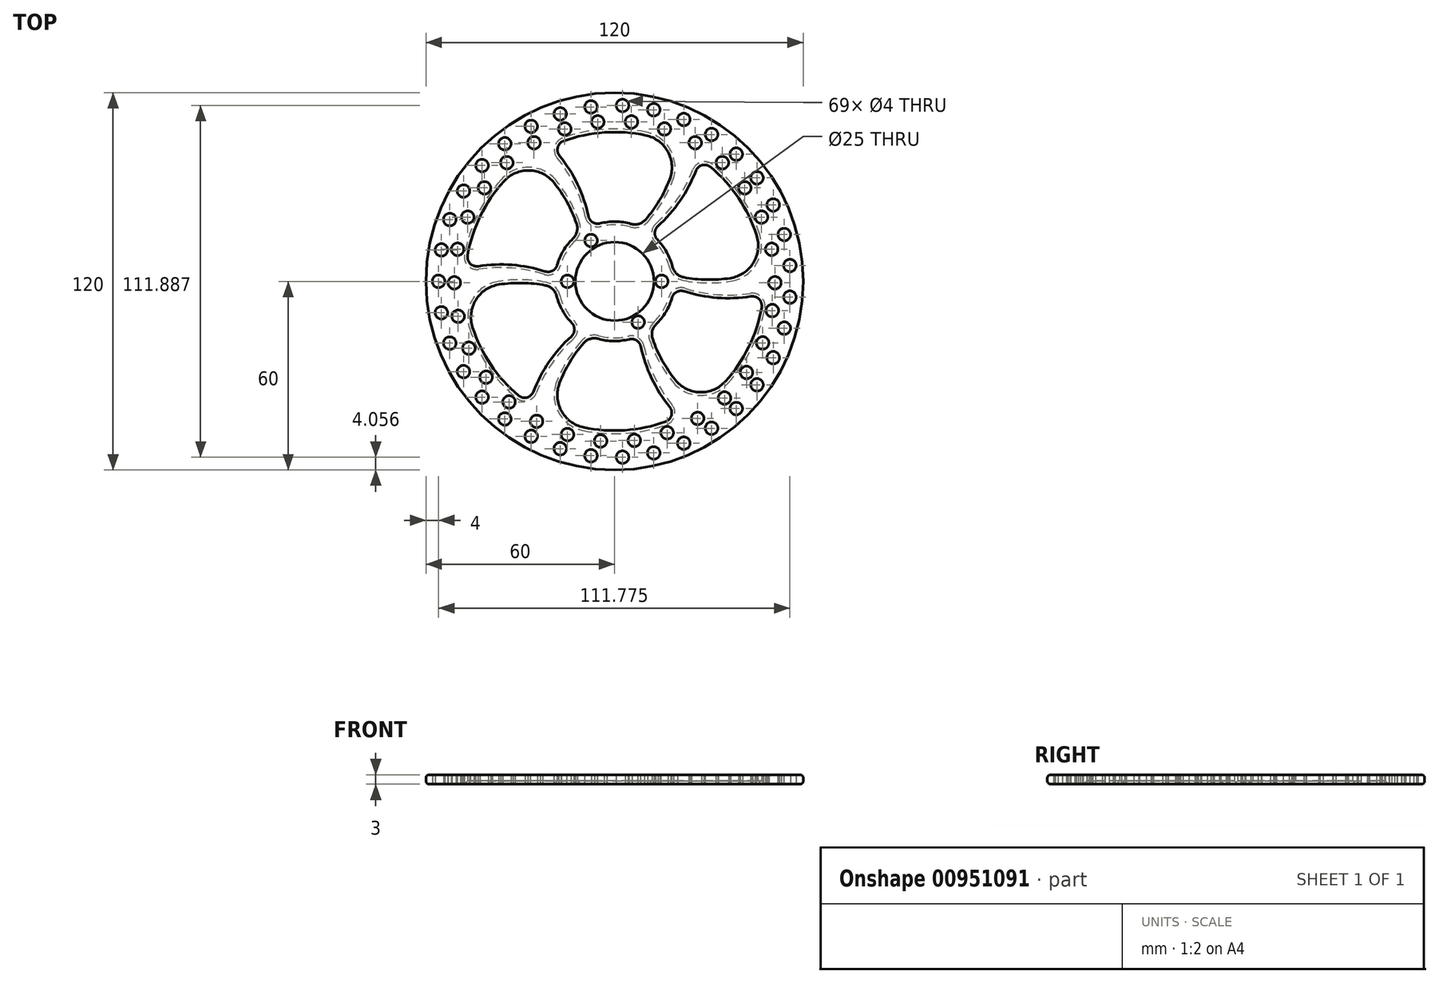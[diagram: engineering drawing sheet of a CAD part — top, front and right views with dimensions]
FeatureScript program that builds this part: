
annotation { "Feature Type Name" : "Feature", "Feature Type Description" : "" }
export const myFeature = defineFeature(function(context is Context, id is Id, definition is map)
    precondition{}
    {
        {
            var Q0;
            Q0=qCreatedBy(makeId("Top.planeOp"),FACE);
            var sketch = newSketch(context, id + "F0", { "sketchPlane" : qUnion([Q0])});
            skCircle(sketch, "E0", {"center": v(0, 0) * mm, "radius": 60 * mm});
            skCircle(sketch, "E1", {"center": v(0, 0) * mm, "radius": 10 * mm});
            skSolve(sketch);
        }
        {
            var Q0;
            Q0=makeQuery(id+"F0.imprint","IMPRINT",FACE,{"disambiguationData":[TD([[makeQuery(id+"F0.imprint","IMPRINT",EDGE,{"derivedFrom":sQuery(id+"F0.wireOp",EDGE,"E0")}),1.0]])]});
            extrude(context, id + "F1", {"entities" : qUnion([Q0]), "depth" : 3 * mm, "offsetDistance" : 25 * mm});
        }
        {
            var Q0;
            Q0=qCreatedBy(makeId("Top.planeOp"),FACE);
            var sketch = newSketch(context, id + "F2", { "sketchPlane" : qUnion([Q0])});
            skCircle(sketch, "E2.4.0", {"center": v(15, 0) * mm, "radius": 2 * mm});
            skPoint(sketch, "E2.center", {"position": v(0, 0) * mm});
            skCircle(sketch, "E3", {"center": v(0, 0) * mm, "radius": 12.5 * mm});
            skCircle(sketch, "E4", {"center": v(0, 0) * mm, "radius": 19 * mm});
            skCircle(sketch, "E5", {"center": v(0, 0) * mm, "radius": 47.5 * mm});
            skPoint(sketch, "E6.startSnap0", {"position": v(0, -18.25) * mm});
            skPoint(sketch, "E6.centerSnap0", {"position": v(0, -18.25) * mm});
            skArc(sketch, "E7", {"start": v(18.9, -2) * mm, "mid": v(32.95, -5.25) * mm, "end": v(47.33, -4) * mm});
            skPoint(sketch, "E8", {"position": v(47.5, 0) * mm});
            skPoint(sketch, "E9", {"position": v(19, 0) * mm});
            skArc(sketch, "E10", {"start": v(18.9, 2) * mm, "mid": v(33.28, 0.62) * mm, "end": v(47.33, 4) * mm});
            skArc(sketch, "E11.1.0", {"start": v(11.18, 15.36) * mm, "mid": v(21.02, 25.91) * mm, "end": v(27.13, 39) * mm});
            skArc(sketch, "E11.1.1", {"start": v(7.72, 17.36) * mm, "mid": v(16.1, 29.13) * mm, "end": v(20.2, 42.99) * mm});
            skArc(sketch, "E11.2.0", {"start": v(-7.72, 17.36) * mm, "mid": v(-11.93, 31.16) * mm, "end": v(-20.2, 43) * mm});
            skArc(sketch, "E11.2.1", {"start": v(-11.18, 15.36) * mm, "mid": v(-17.18, 28.5) * mm, "end": v(-27.13, 39) * mm});
            skArc(sketch, "E11.3.0", {"start": v(-18.9, 2) * mm, "mid": v(-32.95, 5.25) * mm, "end": v(-47.33, 4) * mm});
            skArc(sketch, "E11.3.1", {"start": v(-18.9, -2) * mm, "mid": v(-33.28, -0.62) * mm, "end": v(-47.33, -4) * mm});
            skArc(sketch, "E11.4.0", {"start": v(-11.18, -15.36) * mm, "mid": v(-21.02, -25.91) * mm, "end": v(-27.13, -39) * mm});
            skArc(sketch, "E11.4.1", {"start": v(-7.72, -17.36) * mm, "mid": v(-16.1, -29.13) * mm, "end": v(-20.2, -42.99) * mm});
            skArc(sketch, "E11.5.0", {"start": v(7.72, -17.36) * mm, "mid": v(11.93, -31.16) * mm, "end": v(20.2, -43) * mm});
            skArc(sketch, "E11.5.1", {"start": v(11.18, -15.36) * mm, "mid": v(17.18, -28.5) * mm, "end": v(27.13, -39) * mm});
            skCircle(sketch, "E12.1.0", {"center": v(7.5, -13) * mm, "radius": 2 * mm});
            skLineSegment(sketch, "E12.anchor1", {"start": v(0, 0) * mm, "end": v(15, 0) * mm, "construction": true});
            skLineSegment(sketch, "E12.anchor2", {"start": v(0, 0) * mm, "end": v(7.5, -13) * mm, "construction": true});
            skArc(sketch, "E13", {"start": v(-14.87, -2) * mm, "mid": v(-7.5, -13) * mm, "end": v(5.7, -13.87) * mm});
            skCircle(sketch, "E14", {"center": v(-15, 0) * mm, "radius": 2 * mm});
            skCircle(sketch, "E15.1.0", {"center": v(-7.5, 13) * mm, "radius": 2 * mm});
            skLineSegment(sketch, "E15.anchor1", {"start": v(0, 0) * mm, "end": v(-15, 0) * mm, "construction": true});
            skLineSegment(sketch, "E15.anchor2", {"start": v(0, 0) * mm, "end": v(-6.5, 11.26) * mm, "construction": true});
            skArc(sketch, "E16.trimOffspring", {"start": v(9.16, -11.88) * mm, "mid": v(13, -7.5) * mm, "end": v(14.87, -2) * mm});
            skArc(sketch, "E17.trimOffspring", {"start": v(14.87, 2) * mm, "mid": v(7.5, 13) * mm, "end": v(-5.7, 13.87) * mm});
            skArc(sketch, "E18.trimOffspring", {"start": v(-9.16, 11.88) * mm, "mid": v(-13, 7.5) * mm, "end": v(-14.87, 2) * mm});
            skSolve(sketch);
        }
        {
            var Q0;
            {var subQ0=sQuery(id+"F2.wireOp",EDGE,"E11.3.1");Q0=makeQuery(id+"F2.imprint","IMPRINT",FACE,{"disambiguationData":[TD([[makeQuery(id+"F2.imprint","IMPRINT",EDGE,{"derivedFrom":subQ0}),1.0]])]});}
            var Q1;
            {var subQ0=sQuery(id+"F2.wireOp",EDGE,"E11.4.1");Q1=makeQuery(id+"F2.imprint","IMPRINT",FACE,{"disambiguationData":[TD([[makeQuery(id+"F2.imprint","IMPRINT",EDGE,{"derivedFrom":subQ0}),1.0]])]});}
            var Q2;
            {var subQ0=sQuery(id+"F2.wireOp",EDGE,"E7");Q2=makeQuery(id+"F2.imprint","IMPRINT",FACE,{"disambiguationData":[TD([[makeQuery(id+"F2.imprint","IMPRINT",EDGE,{"derivedFrom":subQ0}),-1.0]])]});}
            var Q3;
            {var subQ0=sQuery(id+"F2.wireOp",EDGE,"E10");Q3=makeQuery(id+"F2.imprint","IMPRINT",FACE,{"disambiguationData":[TD([[makeQuery(id+"F2.imprint","IMPRINT",EDGE,{"derivedFrom":subQ0}),1.0]])]});}
            var Q4;
            {var subQ0=sQuery(id+"F2.wireOp",EDGE,"E11.1.1");Q4=makeQuery(id+"F2.imprint","IMPRINT",FACE,{"disambiguationData":[TD([[makeQuery(id+"F2.imprint","IMPRINT",EDGE,{"derivedFrom":subQ0}),1.0]])]});}
            var Q5;
            {var subQ0=sQuery(id+"F2.wireOp",EDGE,"E11.2.1");Q5=makeQuery(id+"F2.imprint","IMPRINT",FACE,{"disambiguationData":[TD([[makeQuery(id+"F2.imprint","IMPRINT",EDGE,{"derivedFrom":subQ0}),1.0]])]});}
            var Q6;
            {var subQ0=sQuery(id+"F2.wireOp",EDGE,"E3");var subQ12=sQuery(id+"F2.wireOp",EDGE,"4318ffa2-251d-41a1-aac9-47d39e21cad0.2.0");var subQ13=makeQuery(id+"F2.imprint","INTERSECT",VERTEX,{"disambiguationData":[OD(1.0)],"derivedFrom":[subQ12,subQ0]});Q6=makeQuery(id+"F2.imprint","IMPRINT",FACE,{"disambiguationData":[TD([[makeQuery(id+"F2.imprint","IMPRINT",EDGE,{"disambiguationData":[TD([[subQ13,-1.0]])],"derivedFrom":subQ0}),1.0]])]});}
            var Q7;
            Q7=makeQuery(id+"F0.imprint","IMPRINT",FACE,{"disambiguationData":[TD([[makeQuery(id+"F0.imprint","IMPRINT",EDGE,{"derivedFrom":sQuery(id+"F0.wireOp",EDGE,"E1")}),1.0]])]});
            extrude(context, id + "F3", {"entities" : qUnion([Q0, Q1, Q2, Q3, Q4, Q5, Q6, Q7]), "operationType" : NewBodyOperationType.REMOVE, "endBound" : BoundingType.SYMMETRIC, "depth" : 6 * mm, "offsetDistance" : 25 * mm});
        }
        {
            var Q0;
            Q0=qCreatedBy(makeId("Top.planeOp"),FACE);
            var sketch = newSketch(context, id + "F4", { "sketchPlane" : qUnion([Q0])});
            skPoint(sketch, "E19.center", {"position": v(0, 0) * mm});
            skLineSegment(sketch, "E20.anchor1", {"start": v(0, 0) * mm, "end": v(-49.05, 0) * mm, "construction": true});
            skLineSegment(sketch, "E20.anchor2", {"start": v(0, 0) * mm, "end": v(-41.78, -29.25) * mm, "construction": true});
            skCircle(sketch, "E21", {"center": v(-56, 0) * mm, "radius": 2 * mm});
            skCircle(sketch, "E22.1.0", {"center": v(-55.1, -10) * mm, "radius": 2 * mm});
            skCircle(sketch, "E22.2.0", {"center": v(-52.43, -19.68) * mm, "radius": 2 * mm});
            skCircle(sketch, "E22.3.0", {"center": v(-48.07, -28.72) * mm, "radius": 2 * mm});
            skCircle(sketch, "E22.4.0", {"center": v(-42.17, -36.84) * mm, "radius": 2 * mm});
            skCircle(sketch, "E22.5.0", {"center": v(-34.92, -43.78) * mm, "radius": 2 * mm});
            skCircle(sketch, "E22.6.0", {"center": v(-26.54, -49.31) * mm, "radius": 2 * mm});
            skCircle(sketch, "E22.7.0", {"center": v(-17.3, -53.26) * mm, "radius": 2 * mm});
            skCircle(sketch, "E22.8.0", {"center": v(-7.52, -55.5) * mm, "radius": 2 * mm});
            skCircle(sketch, "E22.9.0", {"center": v(2.51, -55.94) * mm, "radius": 2 * mm});
            skCircle(sketch, "E22.10.0", {"center": v(12.46, -54.6) * mm, "radius": 2 * mm});
            skCircle(sketch, "E22.11.0", {"center": v(22, -51.5) * mm, "radius": 2 * mm});
            skCircle(sketch, "E23.1.12.0", {"center": v(30.85, -46.74) * mm, "radius": 2 * mm});
            skCircle(sketch, "E23.1.13.0", {"center": v(38.7, -40.48) * mm, "radius": 2 * mm});
            skCircle(sketch, "E23.1.14.0", {"center": v(45.3, -32.92) * mm, "radius": 2 * mm});
            skCircle(sketch, "E24.1.15.0", {"center": v(50.45, -24.3) * mm, "radius": 2 * mm});
            skCircle(sketch, "E24.1.16.0", {"center": v(53.98, -14.9) * mm, "radius": 2 * mm});
            skCircle(sketch, "E24.1.17.0", {"center": v(55.77, -5.02) * mm, "radius": 2 * mm});
            skCircle(sketch, "E24.1.18.0", {"center": v(55.77, 5.02) * mm, "radius": 2 * mm});
            skCircle(sketch, "E24.1.19.0", {"center": v(53.98, 14.9) * mm, "radius": 2 * mm});
            skCircle(sketch, "E25.1.20.0", {"center": v(50.45, 24.3) * mm, "radius": 2 * mm});
            skCircle(sketch, "E25.1.21.0", {"center": v(45.3, 32.92) * mm, "radius": 2 * mm});
            skCircle(sketch, "E25.1.22.0", {"center": v(38.7, 40.48) * mm, "radius": 2 * mm});
            skCircle(sketch, "E26.1.23.0", {"center": v(30.85, 46.74) * mm, "radius": 2 * mm});
            skCircle(sketch, "E26.1.24.0", {"center": v(22, 51.5) * mm, "radius": 2 * mm});
            skCircle(sketch, "E27.1.25.0", {"center": v(12.46, 54.6) * mm, "radius": 2 * mm});
            skCircle(sketch, "E27.1.26.0", {"center": v(2.51, 55.94) * mm, "radius": 2 * mm});
            skCircle(sketch, "E28.1.27.0", {"center": v(-7.52, 55.5) * mm, "radius": 2 * mm});
            skCircle(sketch, "E28.1.28.0", {"center": v(-17.3, 53.26) * mm, "radius": 2 * mm});
            skCircle(sketch, "E28.1.29.0", {"center": v(-26.54, 49.31) * mm, "radius": 2 * mm});
            skCircle(sketch, "E29.1.30.0", {"center": v(-34.92, 43.78) * mm, "radius": 2 * mm});
            skCircle(sketch, "E29.1.31.0", {"center": v(-42.17, 36.84) * mm, "radius": 2 * mm});
            skCircle(sketch, "E29.1.32.0", {"center": v(-48.07, 28.72) * mm, "radius": 2 * mm});
            skCircle(sketch, "E29.1.33.0", {"center": v(-52.43, 19.68) * mm, "radius": 2 * mm});
            skCircle(sketch, "E29.1.34.0", {"center": v(-55.1, 10) * mm, "radius": 2 * mm});
            skCircle(sketch, "E30.1.17.0", {"center": v(50.14, -9.3) * mm, "radius": 2 * mm});
            skCircle(sketch, "E31.1.0", {"center": v(47.09, -19.59) * mm, "radius": 2 * mm});
            skCircle(sketch, "E31.2.0", {"center": v(41.95, -29) * mm, "radius": 2 * mm});
            skCircle(sketch, "E31.3.0", {"center": v(34.96, -37.13) * mm, "radius": 2 * mm});
            skCircle(sketch, "E31.4.0", {"center": v(26.42, -43.62) * mm, "radius": 2 * mm});
            skCircle(sketch, "E31.5.0", {"center": v(16.72, -48.18) * mm, "radius": 2 * mm});
            skCircle(sketch, "E31.6.0", {"center": v(6.28, -50.61) * mm, "radius": 2 * mm});
            skCircle(sketch, "E31.7.0", {"center": v(-4.44, -50.8) * mm, "radius": 2 * mm});
            skCircle(sketch, "E31.8.0", {"center": v(-14.97, -48.75) * mm, "radius": 2 * mm});
            skCircle(sketch, "E31.9.0", {"center": v(-24.83, -44.55) * mm, "radius": 2 * mm});
            skCircle(sketch, "E31.10.0", {"center": v(-33.6, -38.37) * mm, "radius": 2 * mm});
            skCircle(sketch, "E31.11.0", {"center": v(-40.88, -30.5) * mm, "radius": 2 * mm});
            skCircle(sketch, "E31.12.0", {"center": v(-46.35, -21.27) * mm, "radius": 2 * mm});
            skCircle(sketch, "E31.13.0", {"center": v(-49.77, -11.11) * mm, "radius": 2 * mm});
            skCircle(sketch, "E31.14.0", {"center": v(-51, -0.46) * mm, "radius": 2 * mm});
            skCircle(sketch, "E31.15.0", {"center": v(-49.97, 10.21) * mm, "radius": 2 * mm});
            skCircle(sketch, "E31.16.0", {"center": v(-46.73, 20.43) * mm, "radius": 2 * mm});
            skCircle(sketch, "E31.17.0", {"center": v(-41.42, 29.75) * mm, "radius": 2 * mm});
            skCircle(sketch, "E31.18.0", {"center": v(-34.29, 37.76) * mm, "radius": 2 * mm});
            skCircle(sketch, "E31.19.0", {"center": v(-25.63, 44.1) * mm, "radius": 2 * mm});
            skCircle(sketch, "E31.20.0", {"center": v(-15.85, 48.48) * mm, "radius": 2 * mm});
            skCircle(sketch, "E31.21.0", {"center": v(-5.36, 50.72) * mm, "radius": 2 * mm});
            skCircle(sketch, "E31.22.0", {"center": v(5.36, 50.72) * mm, "radius": 2 * mm});
            skCircle(sketch, "E31.23.0", {"center": v(15.85, 48.48) * mm, "radius": 2 * mm});
            skCircle(sketch, "E31.24.0", {"center": v(25.63, 44.1) * mm, "radius": 2 * mm});
            skCircle(sketch, "E31.25.0", {"center": v(34.29, 37.76) * mm, "radius": 2 * mm});
            skCircle(sketch, "E31.26.0", {"center": v(41.42, 29.75) * mm, "radius": 2 * mm});
            skCircle(sketch, "E31.27.0", {"center": v(46.73, 20.43) * mm, "radius": 2 * mm});
            skCircle(sketch, "E31.28.0", {"center": v(49.97, 10.21) * mm, "radius": 2 * mm});
            skCircle(sketch, "E31.29.0", {"center": v(51, -0.46) * mm, "radius": 2 * mm});
            skLineSegment(sketch, "E31.anchor1", {"start": v(0, 0) * mm, "end": v(50.14, -9.3) * mm, "construction": true});
            skLineSegment(sketch, "E31.anchor2", {"start": v(0, 0) * mm, "end": v(51, -0.46) * mm, "construction": true});
            skSolve(sketch);
        }
        {
            var Q0;
            Q0 = qSketchRegion(id + "F4", true);
            extrude(context, id + "F5", {"entities" : qUnion([Q0]), "operationType" : NewBodyOperationType.REMOVE, "endBound" : BoundingType.UP_TO_NEXT, "depth" : 25 * mm, "offsetDistance" : 25 * mm});
        }
        {
            var Q0;
            Q0=makeQuery(id+"F3.boolean.opBoolean","COPY",EDGE,{"derivedFrom":makeQuery(id+"F3.opExtrude","SWEPT_EDGE",EDGE,{"disambiguationData":[OSD([sQuery(id+"F2.wireOp",EDGE,"E5"),sQuery(id+"F2.wireOp",EDGE,"E11.3.0")])]})});
            var Q1;
            Q1=makeQuery(id+"F3.boolean.opBoolean","COPY",EDGE,{"derivedFrom":makeQuery(id+"F3.opExtrude","SWEPT_EDGE",EDGE,{"disambiguationData":[OSD([sQuery(id+"F2.wireOp",EDGE,"E4"),sQuery(id+"F2.wireOp",EDGE,"E11.3.0")])]})});
            var Q2;
            Q2=makeQuery(id+"F3.boolean.opBoolean","COPY",EDGE,{"derivedFrom":makeQuery(id+"F3.opExtrude","SWEPT_EDGE",EDGE,{"disambiguationData":[OSD([sQuery(id+"F2.wireOp",EDGE,"E4"),sQuery(id+"F2.wireOp",EDGE,"E11.2.0")])]})});
            var Q3;
            Q3=makeQuery(id+"F3.boolean.opBoolean","COPY",EDGE,{"derivedFrom":makeQuery(id+"F3.opExtrude","SWEPT_EDGE",EDGE,{"disambiguationData":[OSD([sQuery(id+"F2.wireOp",EDGE,"E5"),sQuery(id+"F2.wireOp",EDGE,"E11.2.0")])]})});
            var Q4;
            Q4=makeQuery(id+"F3.boolean.opBoolean","COPY",EDGE,{"derivedFrom":makeQuery(id+"F3.opExtrude","SWEPT_EDGE",EDGE,{"disambiguationData":[OSD([sQuery(id+"F2.wireOp",EDGE,"E5"),sQuery(id+"F2.wireOp",EDGE,"E11.1.0")])]})});
            var Q5;
            Q5=makeQuery(id+"F3.boolean.opBoolean","COPY",EDGE,{"derivedFrom":makeQuery(id+"F3.opExtrude","SWEPT_EDGE",EDGE,{"disambiguationData":[OSD([sQuery(id+"F2.wireOp",EDGE,"E4"),sQuery(id+"F2.wireOp",EDGE,"E11.1.0")])]})});
            var Q6;
            Q6=makeQuery(id+"F3.boolean.opBoolean","COPY",EDGE,{"derivedFrom":makeQuery(id+"F3.opExtrude","SWEPT_EDGE",EDGE,{"disambiguationData":[OSD([sQuery(id+"F2.wireOp",EDGE,"E4"),sQuery(id+"F2.wireOp",EDGE,"E7")])]})});
            var Q7;
            Q7=makeQuery(id+"F3.boolean.opBoolean","COPY",EDGE,{"derivedFrom":makeQuery(id+"F3.opExtrude","SWEPT_EDGE",EDGE,{"disambiguationData":[OSD([sQuery(id+"F2.wireOp",EDGE,"E5"),sQuery(id+"F2.wireOp",EDGE,"E7")])]})});
            var Q8;
            Q8=makeQuery(id+"F3.boolean.opBoolean","COPY",EDGE,{"derivedFrom":makeQuery(id+"F3.opExtrude","SWEPT_EDGE",EDGE,{"disambiguationData":[OSD([sQuery(id+"F2.wireOp",EDGE,"E4"),sQuery(id+"F2.wireOp",EDGE,"E11.5.0")])]})});
            var Q9;
            Q9=makeQuery(id+"F3.boolean.opBoolean","COPY",EDGE,{"derivedFrom":makeQuery(id+"F3.opExtrude","SWEPT_EDGE",EDGE,{"disambiguationData":[OSD([sQuery(id+"F2.wireOp",EDGE,"E5"),sQuery(id+"F2.wireOp",EDGE,"E11.5.0")])]})});
            var Q10;
            Q10=makeQuery(id+"F3.boolean.opBoolean","COPY",EDGE,{"derivedFrom":makeQuery(id+"F3.opExtrude","SWEPT_EDGE",EDGE,{"disambiguationData":[OSD([sQuery(id+"F2.wireOp",EDGE,"E4"),sQuery(id+"F2.wireOp",EDGE,"E11.4.0")])]})});
            var Q11;
            Q11=makeQuery(id+"F3.boolean.opBoolean","COPY",EDGE,{"derivedFrom":makeQuery(id+"F3.opExtrude","SWEPT_EDGE",EDGE,{"disambiguationData":[OSD([sQuery(id+"F2.wireOp",EDGE,"E5"),sQuery(id+"F2.wireOp",EDGE,"E11.4.0")])]})});
            fillet(context, id + "F6", {"entities" : qUnion([Q0, Q1, Q2, Q3, Q4, Q5, Q6, Q7, Q8, Q9, Q10, Q11]), "radius" : 3 * mm, "tangentPropagation" : true, "allowEdgeOverflow" : false});
        }
        {
            var Q0;
            Q0=makeQuery(id+"F3.boolean.opBoolean","COPY",EDGE,{"derivedFrom":makeQuery(id+"F3.opExtrude","SWEPT_EDGE",EDGE,{"disambiguationData":[OSD([sQuery(id+"F2.wireOp",EDGE,"E5"),sQuery(id+"F2.wireOp",EDGE,"E11.4.1")])]})});
            var Q1;
            Q1=makeQuery(id+"F3.boolean.opBoolean","COPY",EDGE,{"derivedFrom":makeQuery(id+"F3.opExtrude","SWEPT_EDGE",EDGE,{"disambiguationData":[OSD([sQuery(id+"F2.wireOp",EDGE,"E5"),sQuery(id+"F2.wireOp",EDGE,"E11.5.1")])]})});
            var Q2;
            Q2=makeQuery(id+"F3.boolean.opBoolean","COPY",EDGE,{"derivedFrom":makeQuery(id+"F3.opExtrude","SWEPT_EDGE",EDGE,{"disambiguationData":[OSD([sQuery(id+"F2.wireOp",EDGE,"E5"),sQuery(id+"F2.wireOp",EDGE,"E10")])]})});
            var Q3;
            Q3=makeQuery(id+"F3.boolean.opBoolean","COPY",EDGE,{"derivedFrom":makeQuery(id+"F3.opExtrude","SWEPT_EDGE",EDGE,{"disambiguationData":[OSD([sQuery(id+"F2.wireOp",EDGE,"E5"),sQuery(id+"F2.wireOp",EDGE,"E11.1.1")])]})});
            var Q4;
            Q4=makeQuery(id+"F3.boolean.opBoolean","COPY",EDGE,{"derivedFrom":makeQuery(id+"F3.opExtrude","SWEPT_EDGE",EDGE,{"disambiguationData":[OSD([sQuery(id+"F2.wireOp",EDGE,"E5"),sQuery(id+"F2.wireOp",EDGE,"E11.2.1")])]})});
            var Q5;
            Q5=makeQuery(id+"F3.boolean.opBoolean","COPY",EDGE,{"derivedFrom":makeQuery(id+"F3.opExtrude","SWEPT_EDGE",EDGE,{"disambiguationData":[OSD([sQuery(id+"F2.wireOp",EDGE,"E5"),sQuery(id+"F2.wireOp",EDGE,"E11.3.1")])]})});
            fillet(context, id + "F7", {"entities" : qUnion([Q0, Q1, Q2, Q3, Q4, Q5]), "radius" : 10.5 * mm, "tangentPropagation" : true, "allowEdgeOverflow" : false});
        }
        {
            var Q0;
            Q0=makeQuery(id+"F3.boolean.opBoolean","COPY",EDGE,{"derivedFrom":makeQuery(id+"F3.opExtrude","SWEPT_EDGE",EDGE,{"disambiguationData":[OSD([sQuery(id+"F2.wireOp",EDGE,"E4"),sQuery(id+"F2.wireOp",EDGE,"E11.3.1")])]})});
            var Q1;
            Q1=makeQuery(id+"F3.boolean.opBoolean","COPY",EDGE,{"derivedFrom":makeQuery(id+"F3.opExtrude","SWEPT_EDGE",EDGE,{"disambiguationData":[OSD([sQuery(id+"F2.wireOp",EDGE,"E4"),sQuery(id+"F2.wireOp",EDGE,"E11.4.1")])]})});
            var Q2;
            Q2=makeQuery(id+"F3.boolean.opBoolean","COPY",EDGE,{"derivedFrom":makeQuery(id+"F3.opExtrude","SWEPT_EDGE",EDGE,{"disambiguationData":[OSD([sQuery(id+"F2.wireOp",EDGE,"E4"),sQuery(id+"F2.wireOp",EDGE,"E11.5.1")])]})});
            var Q3;
            Q3=makeQuery(id+"F3.boolean.opBoolean","COPY",EDGE,{"derivedFrom":makeQuery(id+"F3.opExtrude","SWEPT_EDGE",EDGE,{"disambiguationData":[OSD([sQuery(id+"F2.wireOp",EDGE,"E4"),sQuery(id+"F2.wireOp",EDGE,"E10")])]})});
            var Q4;
            Q4=makeQuery(id+"F3.boolean.opBoolean","COPY",EDGE,{"derivedFrom":makeQuery(id+"F3.opExtrude","SWEPT_EDGE",EDGE,{"disambiguationData":[OSD([sQuery(id+"F2.wireOp",EDGE,"E4"),sQuery(id+"F2.wireOp",EDGE,"E11.1.1")])]})});
            var Q5;
            Q5=makeQuery(id+"F3.boolean.opBoolean","COPY",EDGE,{"derivedFrom":makeQuery(id+"F3.opExtrude","SWEPT_EDGE",EDGE,{"disambiguationData":[OSD([sQuery(id+"F2.wireOp",EDGE,"E4"),sQuery(id+"F2.wireOp",EDGE,"E11.2.1")])]})});
            fillet(context, id + "F8", {"entities" : qUnion([Q0, Q1, Q2, Q3, Q4, Q5]), "radius" : 4.5 * mm, "tangentPropagation" : true, "allowEdgeOverflow" : false});
        }
        {
            var Q0;
            Q0=makeQuery(id+"F1.opExtrude","CAP_EDGE",EDGE,{"disambiguationData":[OSD([sQuery(id+"F0.wireOp",EDGE,"E0")])],"isStart":true});
            fillet(context, id + "F9", {"entities" : qUnion([Q0]), "radius" : 1 * mm, "tangentPropagation" : true, "allowEdgeOverflow" : false});
        }
        {
            var Q0;
            Q0=makeQuery(id+"F1.opExtrude","CAP_EDGE",EDGE,{"disambiguationData":[OSD([sQuery(id+"F0.wireOp",EDGE,"E0")])],"isStart":false});
            fillet(context, id + "F10", {"entities" : qUnion([Q0]), "radius" : 1 * mm, "tangentPropagation" : true, "allowEdgeOverflow" : false});
        }
        {
            var Q0;
            {var subQ0=sQuery(id+"F2.wireOp",EDGE,"E5");Q0=makeQuery(id+"F3.boolean.opBoolean","INTERSECT",EDGE,{"derivedFrom":[makeQuery(id+"F1.opExtrude","CAP_FACE",FACE,{"disambiguationData":[OSD([sQuery(id+"F0.wireOp",EDGE,"E0"),sQuery(id+"F0.wireOp",EDGE,"E1")])],"isStart":true}),makeQuery(id+"F3.opExtrude","SWEPT_FACE",FACE,{"disambiguationData":[OSD([subQ0]),TDD([makeQuery(id+"F2.imprint","IMPRINT",EDGE,{"disambiguationData":[TD([[makeQuery(id+"F2.imprint","INTERSECT",VERTEX,{"derivedFrom":[subQ0,sQuery(id+"F2.wireOp",EDGE,"E7")]}),1.0]])],"derivedFrom":subQ0})])]})]});}
            chamfer(context, id + "F11", {"entities" : qUnion([Q0]), "width" : 1 * mm, "tangentPropagation" : true});
        }
        {
            var Q0;
            {var subQ0=sQuery(id+"F2.wireOp",EDGE,"E5");Q0=makeQuery(id+"F3.boolean.opBoolean","INTERSECT",EDGE,{"derivedFrom":[makeQuery(id+"F1.opExtrude","CAP_FACE",FACE,{"disambiguationData":[OSD([sQuery(id+"F0.wireOp",EDGE,"E0"),sQuery(id+"F0.wireOp",EDGE,"E1")])],"isStart":true}),makeQuery(id+"F3.opExtrude","SWEPT_FACE",FACE,{"disambiguationData":[OSD([subQ0]),TDD([makeQuery(id+"F2.imprint","IMPRINT",EDGE,{"disambiguationData":[TD([[makeQuery(id+"F2.imprint","INTERSECT",VERTEX,{"derivedFrom":[subQ0,sQuery(id+"F2.wireOp",EDGE,"E11.4.1")]}),-1.0]])],"derivedFrom":subQ0})])]})]});}
            var Q1;
            Q1=makeQuery(id+"F3.boolean.opBoolean","INTERSECT",EDGE,{"derivedFrom":[makeQuery(id+"F1.opExtrude","CAP_FACE",FACE,{"disambiguationData":[OSD([sQuery(id+"F0.wireOp",EDGE,"E0"),sQuery(id+"F0.wireOp",EDGE,"E1")])],"isStart":true}),makeQuery(id+"F3.opExtrude","SWEPT_FACE",FACE,{"disambiguationData":[OSD([sQuery(id+"F2.wireOp",EDGE,"E11.4.0")])]})]});
            var Q2;
            Q2=makeQuery(id+"F3.boolean.opBoolean","INTERSECT",EDGE,{"derivedFrom":[makeQuery(id+"F1.opExtrude","CAP_FACE",FACE,{"disambiguationData":[OSD([sQuery(id+"F0.wireOp",EDGE,"E0"),sQuery(id+"F0.wireOp",EDGE,"E1")])],"isStart":true}),makeQuery(id+"F3.opExtrude","SWEPT_FACE",FACE,{"disambiguationData":[OSD([sQuery(id+"F2.wireOp",EDGE,"E10")])]})]});
            var Q3;
            Q3=makeQuery(id+"F3.boolean.opBoolean","INTERSECT",EDGE,{"derivedFrom":[makeQuery(id+"F1.opExtrude","CAP_FACE",FACE,{"disambiguationData":[OSD([sQuery(id+"F0.wireOp",EDGE,"E0"),sQuery(id+"F0.wireOp",EDGE,"E1")])],"isStart":true}),makeQuery(id+"F3.opExtrude","SWEPT_FACE",FACE,{"disambiguationData":[OSD([sQuery(id+"F2.wireOp",EDGE,"E11.1.1")])]})]});
            var Q4;
            Q4=makeQuery(id+"F3.boolean.opBoolean","INTERSECT",EDGE,{"derivedFrom":[makeQuery(id+"F1.opExtrude","CAP_FACE",FACE,{"disambiguationData":[OSD([sQuery(id+"F0.wireOp",EDGE,"E0"),sQuery(id+"F0.wireOp",EDGE,"E1")])],"isStart":true}),makeQuery(id+"F3.opExtrude","SWEPT_FACE",FACE,{"disambiguationData":[OSD([sQuery(id+"F2.wireOp",EDGE,"E11.2.1")])]})]});
            chamfer(context, id + "F12", {"entities" : qUnion([Q0, Q1, Q2, Q3, Q4]), "width" : 1 * mm, "tangentPropagation" : true});
        }
        {
            var Q0;
            Q0=makeQuery(id+"F5.boolean.opBoolean","COPY",EDGE,{"derivedFrom":makeQuery(id+"F5.opExtrude","CAP_EDGE",EDGE,{"disambiguationData":[OSD([sQuery(id+"F4.wireOp",EDGE,"E31.13.0")])],"isStart":true})});
            var Q1;
            Q1=makeQuery(id+"F5.boolean.opBoolean","COPY",EDGE,{"derivedFrom":makeQuery(id+"F5.opExtrude","CAP_EDGE",EDGE,{"disambiguationData":[OSD([sQuery(id+"F4.wireOp",EDGE,"E22.2.0")])],"isStart":true})});
            var Q2;
            Q2=makeQuery(id+"F5.boolean.opBoolean","COPY",EDGE,{"derivedFrom":makeQuery(id+"F5.opExtrude","CAP_EDGE",EDGE,{"disambiguationData":[OSD([sQuery(id+"F4.wireOp",EDGE,"E31.12.0")])],"isStart":true})});
            var Q3;
            Q3=makeQuery(id+"F5.boolean.opBoolean","COPY",EDGE,{"derivedFrom":makeQuery(id+"F5.opExtrude","CAP_EDGE",EDGE,{"disambiguationData":[OSD([sQuery(id+"F4.wireOp",EDGE,"E31.11.0")])],"isStart":true})});
            var Q4;
            Q4=makeQuery(id+"F5.boolean.opBoolean","COPY",EDGE,{"derivedFrom":makeQuery(id+"F5.opExtrude","CAP_EDGE",EDGE,{"disambiguationData":[OSD([sQuery(id+"F4.wireOp",EDGE,"E22.3.0")])],"isStart":true})});
            var Q5;
            Q5=makeQuery(id+"F5.boolean.opBoolean","COPY",EDGE,{"derivedFrom":makeQuery(id+"F5.opExtrude","CAP_EDGE",EDGE,{"disambiguationData":[OSD([sQuery(id+"F4.wireOp",EDGE,"E22.4.0")])],"isStart":true})});
            var Q6;
            Q6=makeQuery(id+"F5.boolean.opBoolean","COPY",EDGE,{"derivedFrom":makeQuery(id+"F5.opExtrude","CAP_EDGE",EDGE,{"disambiguationData":[OSD([sQuery(id+"F4.wireOp",EDGE,"E22.5.0")])],"isStart":true})});
            var Q7;
            Q7=makeQuery(id+"F5.boolean.opBoolean","COPY",EDGE,{"derivedFrom":makeQuery(id+"F5.opExtrude","CAP_EDGE",EDGE,{"disambiguationData":[OSD([sQuery(id+"F4.wireOp",EDGE,"E31.10.0")])],"isStart":true})});
            var Q8;
            Q8=makeQuery(id+"F5.boolean.opBoolean","COPY",EDGE,{"derivedFrom":makeQuery(id+"F5.opExtrude","CAP_EDGE",EDGE,{"disambiguationData":[OSD([sQuery(id+"F4.wireOp",EDGE,"E22.6.0")])],"isStart":true})});
            var Q9;
            Q9=makeQuery(id+"F5.boolean.opBoolean","COPY",EDGE,{"derivedFrom":makeQuery(id+"F5.opExtrude","CAP_EDGE",EDGE,{"disambiguationData":[OSD([sQuery(id+"F4.wireOp",EDGE,"E31.9.0")])],"isStart":true})});
            var Q10;
            Q10=makeQuery(id+"F5.boolean.opBoolean","COPY",EDGE,{"derivedFrom":makeQuery(id+"F5.opExtrude","CAP_EDGE",EDGE,{"disambiguationData":[OSD([sQuery(id+"F4.wireOp",EDGE,"E31.8.0")])],"isStart":true})});
            var Q11;
            Q11=makeQuery(id+"F5.boolean.opBoolean","COPY",EDGE,{"derivedFrom":makeQuery(id+"F5.opExtrude","CAP_EDGE",EDGE,{"disambiguationData":[OSD([sQuery(id+"F4.wireOp",EDGE,"E22.8.0")])],"isStart":true})});
            var Q12;
            Q12=makeQuery(id+"F5.boolean.opBoolean","COPY",EDGE,{"derivedFrom":makeQuery(id+"F5.opExtrude","CAP_EDGE",EDGE,{"disambiguationData":[OSD([sQuery(id+"F4.wireOp",EDGE,"E31.7.0")])],"isStart":true})});
            var Q13;
            Q13=makeQuery(id+"F5.boolean.opBoolean","COPY",EDGE,{"derivedFrom":makeQuery(id+"F5.opExtrude","CAP_EDGE",EDGE,{"disambiguationData":[OSD([sQuery(id+"F4.wireOp",EDGE,"E22.9.0")])],"isStart":true})});
            var Q14;
            Q14=makeQuery(id+"F5.boolean.opBoolean","COPY",EDGE,{"derivedFrom":makeQuery(id+"F5.opExtrude","CAP_EDGE",EDGE,{"disambiguationData":[OSD([sQuery(id+"F4.wireOp",EDGE,"E31.6.0")])],"isStart":true})});
            var Q15;
            Q15=makeQuery(id+"F5.boolean.opBoolean","COPY",FACE,{"derivedFrom":makeQuery(id+"F5.opExtrude","SWEPT_FACE",FACE,{"disambiguationData":[OSD([sQuery(id+"F4.wireOp",EDGE,"E22.10.0")])]})});
            var Q16;
            Q16=makeQuery(id+"F5.boolean.opBoolean","COPY",FACE,{"derivedFrom":makeQuery(id+"F5.opExtrude","SWEPT_FACE",FACE,{"disambiguationData":[OSD([sQuery(id+"F4.wireOp",EDGE,"E31.6.0")])]})});
            var Q17;
            Q17=makeQuery(id+"F5.boolean.opBoolean","COPY",EDGE,{"derivedFrom":makeQuery(id+"F5.opExtrude","CAP_EDGE",EDGE,{"disambiguationData":[OSD([sQuery(id+"F4.wireOp",EDGE,"E22.9.0")])],"isStart":false})});
            var Q18;
            Q18=makeQuery(id+"F5.boolean.opBoolean","COPY",FACE,{"derivedFrom":makeQuery(id+"F5.opExtrude","SWEPT_FACE",FACE,{"disambiguationData":[OSD([sQuery(id+"F4.wireOp",EDGE,"E31.7.0")])]})});
            var Q19;
            Q19=makeQuery(id+"F5.boolean.opBoolean","COPY",FACE,{"derivedFrom":makeQuery(id+"F5.opExtrude","SWEPT_FACE",FACE,{"disambiguationData":[OSD([sQuery(id+"F4.wireOp",EDGE,"E22.8.0")])]})});
            var Q20;
            Q20=makeQuery(id+"F5.boolean.opBoolean","COPY",EDGE,{"derivedFrom":makeQuery(id+"F5.opExtrude","CAP_EDGE",EDGE,{"disambiguationData":[OSD([sQuery(id+"F4.wireOp",EDGE,"E22.7.0")])],"isStart":false})});
            var Q21;
            Q21=makeQuery(id+"F5.boolean.opBoolean","COPY",EDGE,{"derivedFrom":makeQuery(id+"F5.opExtrude","CAP_EDGE",EDGE,{"disambiguationData":[OSD([sQuery(id+"F4.wireOp",EDGE,"E22.6.0")])],"isStart":false})});
            var Q22;
            Q22=makeQuery(id+"F5.boolean.opBoolean","COPY",EDGE,{"derivedFrom":makeQuery(id+"F5.opExtrude","CAP_EDGE",EDGE,{"disambiguationData":[OSD([sQuery(id+"F4.wireOp",EDGE,"E31.9.0")])],"isStart":false})});
            var Q23;
            Q23=makeQuery(id+"F5.boolean.opBoolean","COPY",EDGE,{"derivedFrom":makeQuery(id+"F5.opExtrude","CAP_EDGE",EDGE,{"disambiguationData":[OSD([sQuery(id+"F4.wireOp",EDGE,"E31.10.0")])],"isStart":false})});
            var Q24;
            Q24=makeQuery(id+"F5.boolean.opBoolean","COPY",EDGE,{"derivedFrom":makeQuery(id+"F5.opExtrude","CAP_EDGE",EDGE,{"disambiguationData":[OSD([sQuery(id+"F4.wireOp",EDGE,"E22.4.0")])],"isStart":false})});
            var Q25;
            Q25=makeQuery(id+"F5.boolean.opBoolean","COPY",FACE,{"derivedFrom":makeQuery(id+"F5.opExtrude","SWEPT_FACE",FACE,{"disambiguationData":[OSD([sQuery(id+"F4.wireOp",EDGE,"E31.11.0")])]})});
            var Q26;
            Q26=makeQuery(id+"F5.boolean.opBoolean","COPY",EDGE,{"derivedFrom":makeQuery(id+"F5.opExtrude","CAP_EDGE",EDGE,{"disambiguationData":[OSD([sQuery(id+"F4.wireOp",EDGE,"E22.3.0")])],"isStart":false})});
            var Q27;
            Q27=makeQuery(id+"F5.boolean.opBoolean","COPY",EDGE,{"derivedFrom":makeQuery(id+"F5.opExtrude","CAP_EDGE",EDGE,{"disambiguationData":[OSD([sQuery(id+"F4.wireOp",EDGE,"E22.2.0")])],"isStart":false})});
            var Q28;
            Q28=makeQuery(id+"F5.boolean.opBoolean","COPY",EDGE,{"derivedFrom":makeQuery(id+"F5.opExtrude","CAP_EDGE",EDGE,{"disambiguationData":[OSD([sQuery(id+"F4.wireOp",EDGE,"E31.12.0")])],"isStart":false})});
            var Q29;
            Q29=makeQuery(id+"F5.boolean.opBoolean","COPY",EDGE,{"derivedFrom":makeQuery(id+"F5.opExtrude","CAP_EDGE",EDGE,{"disambiguationData":[OSD([sQuery(id+"F4.wireOp",EDGE,"E31.13.0")])],"isStart":false})});
            var Q30;
            Q30=makeQuery(id+"F5.boolean.opBoolean","COPY",EDGE,{"derivedFrom":makeQuery(id+"F5.opExtrude","CAP_EDGE",EDGE,{"disambiguationData":[OSD([sQuery(id+"F4.wireOp",EDGE,"E22.1.0")])],"isStart":false})});
            var Q31;
            Q31=makeQuery(id+"F5.boolean.opBoolean","COPY",EDGE,{"derivedFrom":makeQuery(id+"F5.opExtrude","CAP_EDGE",EDGE,{"disambiguationData":[OSD([sQuery(id+"F4.wireOp",EDGE,"E22.1.0")])],"isStart":true})});
            var Q32;
            Q32=makeQuery(id+"F5.boolean.opBoolean","COPY",FACE,{"derivedFrom":makeQuery(id+"F5.opExtrude","SWEPT_FACE",FACE,{"disambiguationData":[OSD([sQuery(id+"F4.wireOp",EDGE,"E21")])]})});
            var Q33;
            Q33=makeQuery(id+"F5.boolean.opBoolean","COPY",FACE,{"derivedFrom":makeQuery(id+"F5.opExtrude","SWEPT_FACE",FACE,{"disambiguationData":[OSD([sQuery(id+"F4.wireOp",EDGE,"E31.14.0")])]})});
            var Q34;
            Q34=makeQuery(id+"F5.boolean.opBoolean","COPY",FACE,{"derivedFrom":makeQuery(id+"F5.opExtrude","SWEPT_FACE",FACE,{"disambiguationData":[OSD([sQuery(id+"F4.wireOp",EDGE,"E31.15.0")])]})});
            var Q35;
            Q35=makeQuery(id+"F5.boolean.opBoolean","COPY",FACE,{"derivedFrom":makeQuery(id+"F5.opExtrude","SWEPT_FACE",FACE,{"disambiguationData":[OSD([sQuery(id+"F4.wireOp",EDGE,"E29.1.34.0")])]})});
            var Q36;
            Q36=makeQuery(id+"F5.boolean.opBoolean","COPY",FACE,{"derivedFrom":makeQuery(id+"F5.opExtrude","SWEPT_FACE",FACE,{"disambiguationData":[OSD([sQuery(id+"F4.wireOp",EDGE,"E29.1.33.0")])]})});
            var Q37;
            Q37=makeQuery(id+"F5.boolean.opBoolean","COPY",FACE,{"derivedFrom":makeQuery(id+"F5.opExtrude","SWEPT_FACE",FACE,{"disambiguationData":[OSD([sQuery(id+"F4.wireOp",EDGE,"E31.16.0")])]})});
            var Q38;
            Q38=makeQuery(id+"F5.boolean.opBoolean","COPY",FACE,{"derivedFrom":makeQuery(id+"F5.opExtrude","SWEPT_FACE",FACE,{"disambiguationData":[OSD([sQuery(id+"F4.wireOp",EDGE,"E29.1.32.0")])]})});
            var Q39;
            Q39=makeQuery(id+"F5.boolean.opBoolean","COPY",FACE,{"derivedFrom":makeQuery(id+"F5.opExtrude","SWEPT_FACE",FACE,{"disambiguationData":[OSD([sQuery(id+"F4.wireOp",EDGE,"E31.17.0")])]})});
            var Q40;
            Q40=makeQuery(id+"F5.boolean.opBoolean","COPY",FACE,{"derivedFrom":makeQuery(id+"F5.opExtrude","SWEPT_FACE",FACE,{"disambiguationData":[OSD([sQuery(id+"F4.wireOp",EDGE,"E31.18.0")])]})});
            var Q41;
            Q41=makeQuery(id+"F5.boolean.opBoolean","COPY",FACE,{"derivedFrom":makeQuery(id+"F5.opExtrude","SWEPT_FACE",FACE,{"disambiguationData":[OSD([sQuery(id+"F4.wireOp",EDGE,"E29.1.31.0")])]})});
            var Q42;
            Q42=makeQuery(id+"F5.boolean.opBoolean","COPY",FACE,{"derivedFrom":makeQuery(id+"F5.opExtrude","SWEPT_FACE",FACE,{"disambiguationData":[OSD([sQuery(id+"F4.wireOp",EDGE,"E29.1.30.0")])]})});
            var Q43;
            Q43=makeQuery(id+"F5.boolean.opBoolean","COPY",FACE,{"derivedFrom":makeQuery(id+"F5.opExtrude","SWEPT_FACE",FACE,{"disambiguationData":[OSD([sQuery(id+"F4.wireOp",EDGE,"E31.5.0")])]})});
            var Q44;
            Q44=makeQuery(id+"F5.boolean.opBoolean","COPY",FACE,{"derivedFrom":makeQuery(id+"F5.opExtrude","SWEPT_FACE",FACE,{"disambiguationData":[OSD([sQuery(id+"F4.wireOp",EDGE,"E22.11.0")])]})});
            fillet(context, id + "F13", {"entities" : qUnion([Q0, Q1, Q2, Q3, Q4, Q5, Q6, Q7, Q8, Q9, Q10, Q11, Q12, Q13, Q14, Q15, Q16, Q17, Q18, Q19, Q20, Q21, Q22, Q23, Q24, Q25, Q26, Q27, Q28, Q29, Q30, Q31, Q32, Q33, Q34, Q35, Q36, Q37, Q38, Q39, Q40, Q41, Q42, Q43, Q44]), "radius" : 0.3 * mm, "tangentPropagation" : true, "allowEdgeOverflow" : false});
        }
        {
            var Q0;
            Q0=makeQuery(id+"F5.boolean.opBoolean","COPY",FACE,{"derivedFrom":makeQuery(id+"F5.opExtrude","SWEPT_FACE",FACE,{"disambiguationData":[OSD([sQuery(id+"F4.wireOp",EDGE,"E22.7.0")])]})});
            var Q1;
            Q1=makeQuery(id+"F5.boolean.opBoolean","COPY",FACE,{"derivedFrom":makeQuery(id+"F5.opExtrude","SWEPT_FACE",FACE,{"disambiguationData":[OSD([sQuery(id+"F4.wireOp",EDGE,"E23.1.12.0")])]})});
            var Q2;
            Q2=makeQuery(id+"F5.boolean.opBoolean","COPY",FACE,{"derivedFrom":makeQuery(id+"F5.opExtrude","SWEPT_FACE",FACE,{"disambiguationData":[OSD([sQuery(id+"F4.wireOp",EDGE,"E31.4.0")])]})});
            var Q3;
            Q3=makeQuery(id+"F5.boolean.opBoolean","COPY",FACE,{"derivedFrom":makeQuery(id+"F5.opExtrude","SWEPT_FACE",FACE,{"disambiguationData":[OSD([sQuery(id+"F4.wireOp",EDGE,"E23.1.13.0")])]})});
            var Q4;
            Q4=makeQuery(id+"F5.boolean.opBoolean","COPY",FACE,{"derivedFrom":makeQuery(id+"F5.opExtrude","SWEPT_FACE",FACE,{"disambiguationData":[OSD([sQuery(id+"F4.wireOp",EDGE,"E31.3.0")])]})});
            var Q5;
            Q5=makeQuery(id+"F5.boolean.opBoolean","COPY",FACE,{"derivedFrom":makeQuery(id+"F5.opExtrude","SWEPT_FACE",FACE,{"disambiguationData":[OSD([sQuery(id+"F4.wireOp",EDGE,"E23.1.14.0")])]})});
            var Q6;
            Q6=makeQuery(id+"F5.boolean.opBoolean","COPY",FACE,{"derivedFrom":makeQuery(id+"F5.opExtrude","SWEPT_FACE",FACE,{"disambiguationData":[OSD([sQuery(id+"F4.wireOp",EDGE,"E31.2.0")])]})});
            var Q7;
            Q7=makeQuery(id+"F5.boolean.opBoolean","COPY",FACE,{"derivedFrom":makeQuery(id+"F5.opExtrude","SWEPT_FACE",FACE,{"disambiguationData":[OSD([sQuery(id+"F4.wireOp",EDGE,"E31.1.0")])]})});
            var Q8;
            Q8=makeQuery(id+"F5.boolean.opBoolean","COPY",FACE,{"derivedFrom":makeQuery(id+"F5.opExtrude","SWEPT_FACE",FACE,{"disambiguationData":[OSD([sQuery(id+"F4.wireOp",EDGE,"E30.1.17.0")])]})});
            var Q9;
            Q9=makeQuery(id+"F5.boolean.opBoolean","COPY",FACE,{"derivedFrom":makeQuery(id+"F5.opExtrude","SWEPT_FACE",FACE,{"disambiguationData":[OSD([sQuery(id+"F4.wireOp",EDGE,"E24.1.16.0")])]})});
            var Q10;
            Q10=makeQuery(id+"F5.boolean.opBoolean","COPY",FACE,{"derivedFrom":makeQuery(id+"F5.opExtrude","SWEPT_FACE",FACE,{"disambiguationData":[OSD([sQuery(id+"F4.wireOp",EDGE,"E24.1.15.0")])]})});
            var Q11;
            Q11=makeQuery(id+"F5.boolean.opBoolean","COPY",FACE,{"derivedFrom":makeQuery(id+"F5.opExtrude","SWEPT_FACE",FACE,{"disambiguationData":[OSD([sQuery(id+"F4.wireOp",EDGE,"E31.29.0")])]})});
            var Q12;
            Q12=makeQuery(id+"F5.boolean.opBoolean","COPY",FACE,{"derivedFrom":makeQuery(id+"F5.opExtrude","SWEPT_FACE",FACE,{"disambiguationData":[OSD([sQuery(id+"F4.wireOp",EDGE,"E24.1.17.0")])]})});
            var Q13;
            Q13=makeQuery(id+"F5.boolean.opBoolean","COPY",FACE,{"derivedFrom":makeQuery(id+"F5.opExtrude","SWEPT_FACE",FACE,{"disambiguationData":[OSD([sQuery(id+"F4.wireOp",EDGE,"E24.1.18.0")])]})});
            var Q14;
            Q14=makeQuery(id+"F5.boolean.opBoolean","COPY",FACE,{"derivedFrom":makeQuery(id+"F5.opExtrude","SWEPT_FACE",FACE,{"disambiguationData":[OSD([sQuery(id+"F4.wireOp",EDGE,"E31.28.0")])]})});
            var Q15;
            Q15=makeQuery(id+"F5.boolean.opBoolean","COPY",FACE,{"derivedFrom":makeQuery(id+"F5.opExtrude","SWEPT_FACE",FACE,{"disambiguationData":[OSD([sQuery(id+"F4.wireOp",EDGE,"E24.1.19.0")])]})});
            var Q16;
            Q16=makeQuery(id+"F5.boolean.opBoolean","COPY",FACE,{"derivedFrom":makeQuery(id+"F5.opExtrude","SWEPT_FACE",FACE,{"disambiguationData":[OSD([sQuery(id+"F4.wireOp",EDGE,"E31.27.0")])]})});
            var Q17;
            Q17=makeQuery(id+"F5.boolean.opBoolean","COPY",FACE,{"derivedFrom":makeQuery(id+"F5.opExtrude","SWEPT_FACE",FACE,{"disambiguationData":[OSD([sQuery(id+"F4.wireOp",EDGE,"E25.1.20.0")])]})});
            var Q18;
            Q18=makeQuery(id+"F5.boolean.opBoolean","COPY",FACE,{"derivedFrom":makeQuery(id+"F5.opExtrude","SWEPT_FACE",FACE,{"disambiguationData":[OSD([sQuery(id+"F4.wireOp",EDGE,"E25.1.21.0")])]})});
            var Q19;
            Q19=makeQuery(id+"F5.boolean.opBoolean","COPY",FACE,{"derivedFrom":makeQuery(id+"F5.opExtrude","SWEPT_FACE",FACE,{"disambiguationData":[OSD([sQuery(id+"F4.wireOp",EDGE,"E31.26.0")])]})});
            var Q20;
            Q20=makeQuery(id+"F5.boolean.opBoolean","COPY",FACE,{"derivedFrom":makeQuery(id+"F5.opExtrude","SWEPT_FACE",FACE,{"disambiguationData":[OSD([sQuery(id+"F4.wireOp",EDGE,"E25.1.22.0")])]})});
            var Q21;
            Q21=makeQuery(id+"F5.boolean.opBoolean","COPY",FACE,{"derivedFrom":makeQuery(id+"F5.opExtrude","SWEPT_FACE",FACE,{"disambiguationData":[OSD([sQuery(id+"F4.wireOp",EDGE,"E31.25.0")])]})});
            var Q22;
            Q22=makeQuery(id+"F5.boolean.opBoolean","COPY",FACE,{"derivedFrom":makeQuery(id+"F5.opExtrude","SWEPT_FACE",FACE,{"disambiguationData":[OSD([sQuery(id+"F4.wireOp",EDGE,"E31.24.0")])]})});
            var Q23;
            Q23=makeQuery(id+"F5.boolean.opBoolean","COPY",FACE,{"derivedFrom":makeQuery(id+"F5.opExtrude","SWEPT_FACE",FACE,{"disambiguationData":[OSD([sQuery(id+"F4.wireOp",EDGE,"E26.1.23.0")])]})});
            var Q24;
            Q24=makeQuery(id+"F5.boolean.opBoolean","COPY",FACE,{"derivedFrom":makeQuery(id+"F5.opExtrude","SWEPT_FACE",FACE,{"disambiguationData":[OSD([sQuery(id+"F4.wireOp",EDGE,"E27.1.25.0")])]})});
            var Q25;
            Q25=makeQuery(id+"F5.boolean.opBoolean","COPY",FACE,{"derivedFrom":makeQuery(id+"F5.opExtrude","SWEPT_FACE",FACE,{"disambiguationData":[OSD([sQuery(id+"F4.wireOp",EDGE,"E26.1.24.0")])]})});
            var Q26;
            Q26=makeQuery(id+"F5.boolean.opBoolean","COPY",FACE,{"derivedFrom":makeQuery(id+"F5.opExtrude","SWEPT_FACE",FACE,{"disambiguationData":[OSD([sQuery(id+"F4.wireOp",EDGE,"E31.23.0")])]})});
            var Q27;
            Q27=makeQuery(id+"F5.boolean.opBoolean","COPY",FACE,{"derivedFrom":makeQuery(id+"F5.opExtrude","SWEPT_FACE",FACE,{"disambiguationData":[OSD([sQuery(id+"F4.wireOp",EDGE,"E27.1.26.0")])]})});
            var Q28;
            Q28=makeQuery(id+"F5.boolean.opBoolean","COPY",FACE,{"derivedFrom":makeQuery(id+"F5.opExtrude","SWEPT_FACE",FACE,{"disambiguationData":[OSD([sQuery(id+"F4.wireOp",EDGE,"E31.22.0")])]})});
            var Q29;
            Q29=makeQuery(id+"F5.boolean.opBoolean","COPY",FACE,{"derivedFrom":makeQuery(id+"F5.opExtrude","SWEPT_FACE",FACE,{"disambiguationData":[OSD([sQuery(id+"F4.wireOp",EDGE,"E28.1.27.0")])]})});
            var Q30;
            Q30=makeQuery(id+"F5.boolean.opBoolean","COPY",FACE,{"derivedFrom":makeQuery(id+"F5.opExtrude","SWEPT_FACE",FACE,{"disambiguationData":[OSD([sQuery(id+"F4.wireOp",EDGE,"E31.21.0")])]})});
            var Q31;
            Q31=makeQuery(id+"F5.boolean.opBoolean","COPY",FACE,{"derivedFrom":makeQuery(id+"F5.opExtrude","SWEPT_FACE",FACE,{"disambiguationData":[OSD([sQuery(id+"F4.wireOp",EDGE,"E28.1.28.0")])]})});
            var Q32;
            Q32=makeQuery(id+"F5.boolean.opBoolean","COPY",FACE,{"derivedFrom":makeQuery(id+"F5.opExtrude","SWEPT_FACE",FACE,{"disambiguationData":[OSD([sQuery(id+"F4.wireOp",EDGE,"E31.20.0")])]})});
            var Q33;
            Q33=makeQuery(id+"F5.boolean.opBoolean","COPY",FACE,{"derivedFrom":makeQuery(id+"F5.opExtrude","SWEPT_FACE",FACE,{"disambiguationData":[OSD([sQuery(id+"F4.wireOp",EDGE,"E28.1.29.0")])]})});
            var Q34;
            Q34=makeQuery(id+"F5.boolean.opBoolean","COPY",FACE,{"derivedFrom":makeQuery(id+"F5.opExtrude","SWEPT_FACE",FACE,{"disambiguationData":[OSD([sQuery(id+"F4.wireOp",EDGE,"E31.19.0")])]})});
            fillet(context, id + "F14", {"entities" : qUnion([Q0, Q1, Q2, Q3, Q4, Q5, Q6, Q7, Q8, Q9, Q10, Q11, Q12, Q13, Q14, Q15, Q16, Q17, Q18, Q19, Q20, Q21, Q22, Q23, Q24, Q25, Q26, Q27, Q28, Q29, Q30, Q31, Q32, Q33, Q34]), "radius" : 0.3 * mm, "tangentPropagation" : true, "allowEdgeOverflow" : false});
        }
        {
            var Q0;
            {var subQ0=sQuery(id+"F2.wireOp",EDGE,"E14");var subQ1=makeQuery(id+"F2.imprint","INTERSECT",VERTEX,{"derivedFrom":[sQuery(id+"F2.wireOp",EDGE,"E13"),subQ0]});Q0=makeQuery(id+"F2.imprint","IMPRINT",FACE,{"disambiguationData":[TD([[makeQuery(id+"F2.imprint","IMPRINT",EDGE,{"disambiguationData":[TD([[subQ1,1.0]])],"derivedFrom":subQ0}),1.0]])]});}
            var Q1;
            {var subQ0=sQuery(id+"F2.wireOp",EDGE,"E2.4.0");var subQ1=makeQuery(id+"F2.imprint","INTERSECT",VERTEX,{"derivedFrom":[subQ0,sQuery(id+"F2.wireOp",EDGE,"E16.trimOffspring")]});Q1=makeQuery(id+"F2.imprint","IMPRINT",FACE,{"disambiguationData":[TD([[makeQuery(id+"F2.imprint","IMPRINT",EDGE,{"disambiguationData":[TD([[subQ1,-1.0]])],"derivedFrom":subQ0}),1.0]])]});}
            var Q2;
            {var subQ0=sQuery(id+"F2.wireOp",EDGE,"E12.1.0");var subQ1=makeQuery(id+"F2.imprint","INTERSECT",VERTEX,{"derivedFrom":[subQ0,sQuery(id+"F2.wireOp",EDGE,"E13")]});Q2=makeQuery(id+"F2.imprint","IMPRINT",FACE,{"disambiguationData":[TD([[makeQuery(id+"F2.imprint","IMPRINT",EDGE,{"disambiguationData":[TD([[subQ1,-1.0]])],"derivedFrom":subQ0}),1.0]])]});}
            var Q3;
            {var subQ0=sQuery(id+"F2.wireOp",EDGE,"E15.1.0");var subQ1=makeQuery(id+"F2.imprint","INTERSECT",VERTEX,{"derivedFrom":[subQ0,sQuery(id+"F2.wireOp",EDGE,"E17.trimOffspring")]});Q3=makeQuery(id+"F2.imprint","IMPRINT",FACE,{"disambiguationData":[TD([[makeQuery(id+"F2.imprint","IMPRINT",EDGE,{"disambiguationData":[TD([[subQ1,-1.0]])],"derivedFrom":subQ0}),1.0]])]});}
            extrude(context, id + "F15", {"entities" : qUnion([Q0, Q1, Q2, Q3]), "operationType" : NewBodyOperationType.REMOVE, "endBound" : BoundingType.UP_TO_NEXT, "depth" : 25 * mm, "offsetDistance" : 25 * mm});
        }
    });
